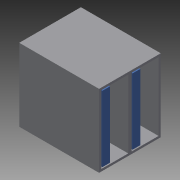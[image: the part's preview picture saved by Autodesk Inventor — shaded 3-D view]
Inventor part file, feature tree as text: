
AUTODESK INVENTOR PART (.ipt)
format: ipt  version: 2013 SP2 (Build 170200200, 200)  size: 124,928 bytes
history: native  units: mm
features: extrude x3, sketch x3, plane x1, pattern_linear x1
ambient origin geometry x8: Origin, YZ Plane, XZ Plane, XY Plane, X Axis, Y Axis, Z Axis, Center Point
bodies: Solid1 (feature_tree)
feature tree (8):
  plane  "Work Plane1"
  extrude  "Extrusion1"  Depth=5.7mm
  extrude  "Extrusion2"  Depth=0.4mm
  extrude  "Extrusion3"  Depth=0.2mm
  pattern_linear  "Rectangular Pattern1"  Spacing1=0.2mm  [1 undecoded]
  sketch  "Sketch1"  dims[d0=14.5mm d2=5.7mm]
  sketch  "Sketch2"  dims[d3=13.2mm d4=0.0mm d5=0.4mm]
  sketch  "Sketch3"  dims[d6=13.0mm d7=0.0mm d8=0.2mm d9=0.2mm d10=0.2mm d11=1.4mm d12=13.0mm d13=0.0mm d14=20.0mm d16=5.5mm]
note: 1 required parameter value undecoded (feature->parameter linkage not recoverable at this tier; creation-order binding heuristic only, values carry confidence <= 0.55)
